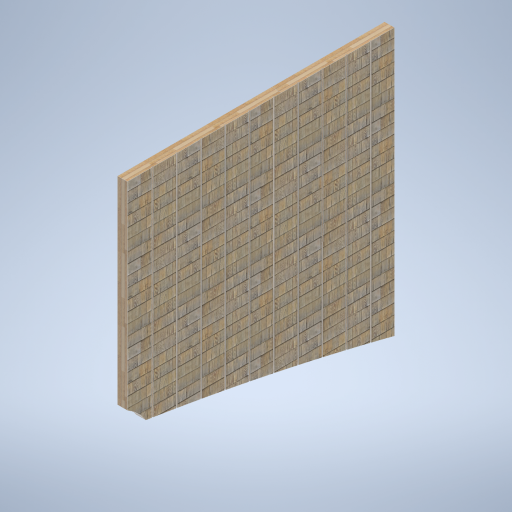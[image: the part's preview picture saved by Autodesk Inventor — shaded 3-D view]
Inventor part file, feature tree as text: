
AUTODESK INVENTOR PART (.ipt)
format: ipt  version: 2024.2 (Build 282272000, 272)  size: 505,856 bytes
history: native  units: mm
features: extrude x2, sketch x2
ambient origin geometry x8: Origin, YZ Plane, XZ Plane, XY Plane, X Axis, Y Axis, Z Axis, Center Point
bodies: Solid1 (feature_tree)
feature tree (4):
  extrude  "Extrusion1"  Depth=350.0mm
  extrude  "Extrusion2"  Depth=20.0mm
  sketch  "Sketch1"  dims[d0=150.0mm d1=0.0mm d2=350.0mm]
  sketch  "Sketch2"  dims[d3=10.0mm d4=20.0mm d5=350.0mm d6=20.0mm d7=350.0mm d8=10.0mm d9=20.0mm d10=350.0mm d11=20.0mm d12=350.0mm d13=350.0mm d14=10.0mm d15=20.0mm d16=350.0mm d17=20.0mm d18=350.0mm d19=20.0mm d20=350.0mm d21=20.0mm d22=350.0mm d23=20.0mm d24=0.0mm d25=0.0mm]
